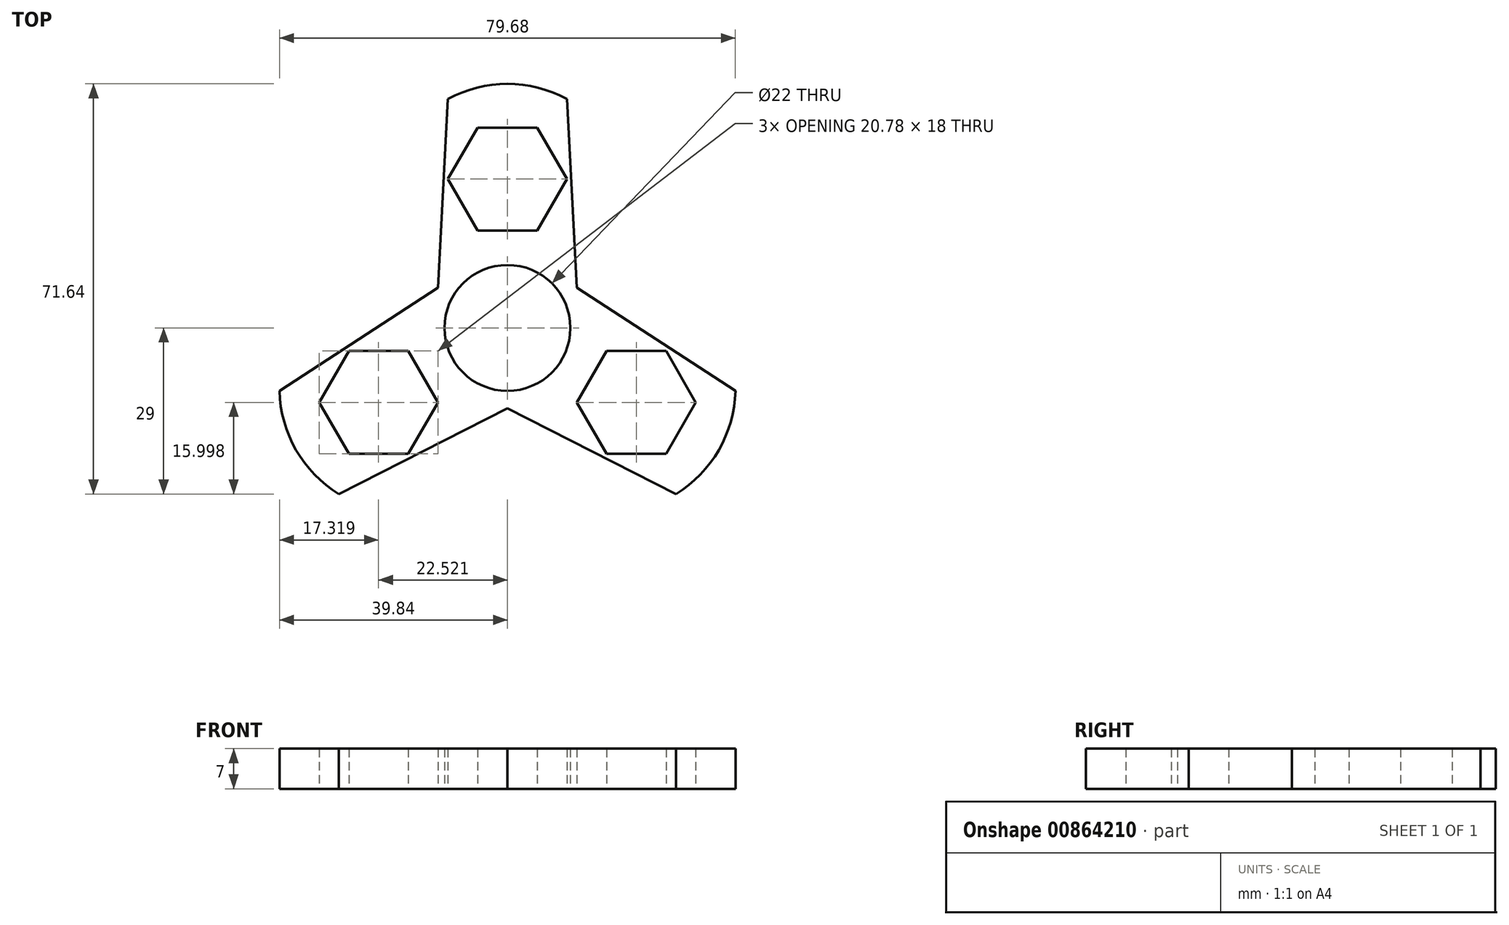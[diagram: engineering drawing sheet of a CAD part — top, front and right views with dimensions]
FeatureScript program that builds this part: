
annotation { "Feature Type Name" : "Feature", "Feature Type Description" : "" }
export const myFeature = defineFeature(function(context is Context, id is Id, definition is map)
    precondition{}
    {
        {
            var Q0;
            Q0=qCreatedBy(makeId("Top.planeOp"),FACE);
            var sketch = newSketch(context, id + "F0", { "sketchPlane" : qUnion([Q0])});
            skCircle(sketch, "E0", {"center": v(0, 0) * mm, "radius": 11 * mm});
            skCircle(sketch, "E1.0", {"center": v(0, 0) * mm, "radius": 14 * mm});
            skCircle(sketch, "E2", {"center": v(0, 0) * mm, "radius": 45 * mm, "construction": true});
            skLineSegment(sketch, "E3", {"start": v(-7.68, 21.31) * mm, "end": v(-7.68, 21.32) * mm});
            skLineSegment(sketch, "E4.MirrorCS", {"start": v(7.68, 21.31) * mm, "end": v(7.68, 21.32) * mm});
            skCircle(sketch, "E5.cCircle", {"center": v(0, 26) * mm, "radius": 9 * mm, "construction": true});
            skPoint(sketch, "E5.cCircle.centerSnap0", {"position": v(6.74, 26) * mm});
            skLineSegment(sketch, "E5.0", {"start": v(-5.2, 35) * mm, "end": v(5.2, 35) * mm});
            skLineSegment(sketch, "E5.1", {"start": v(5.2, 35) * mm, "end": v(10.4, 26) * mm});
            skLineSegment(sketch, "E5.2", {"start": v(10.4, 26) * mm, "end": v(5.2, 17) * mm});
            skLineSegment(sketch, "E5.3", {"start": v(5.2, 17) * mm, "end": v(-5.2, 17) * mm});
            skLineSegment(sketch, "E5.4", {"start": v(-5.2, 17) * mm, "end": v(-10.4, 26) * mm});
            skLineSegment(sketch, "E5.5", {"start": v(-10.4, 26) * mm, "end": v(-5.2, 35) * mm});
            skPoint(sketch, "E5.0.midPoint", {"position": v(0, 35) * mm});
            skLineSegment(sketch, "E6.trimOffspring", {"start": v(-5.28, 33.3) * mm, "end": v(-4.93, 35) * mm});
            skLineSegment(sketch, "E7.trimOffspring", {"start": v(5.28, 33.3) * mm, "end": v(4.93, 35) * mm});
            skPoint(sketch, "E8.start.orphan", {"position": v(-3.48, 42.2) * mm});
            skPoint(sketch, "E9.orphan", {"position": v(-10, 9.8) * mm});
            skPoint(sketch, "E10.orphan", {"position": v(10, 9.8) * mm});
            skPoint(sketch, "E11.orphan", {"position": v(3.48, 42.2) * mm});
            skPoint(sketch, "E12.end.orphan", {"position": v(-10.4, 40) * mm});
            skLineSegment(sketch, "E13", {"start": v(-12.15, 6.96) * mm, "end": v(-10.4, 40) * mm});
            skLineSegment(sketch, "E14.MirrorCS", {"start": v(12.15, 6.96) * mm, "end": v(10.4, 40) * mm});
            skArc(sketch, "E15", {"start": v(10.4, 40) * mm, "mid": v(0, 42.64) * mm, "end": v(-10.4, 40) * mm});
            skCircle(sketch, "E16.1.0", {"center": v(-22.52, -13) * mm, "radius": 9 * mm, "construction": true});
            skArc(sketch, "E16.1.1", {"start": v(-39.84, -11) * mm, "mid": v(-36.93, -21.32) * mm, "end": v(-29.45, -29) * mm});
            skLineSegment(sketch, "E16.1.2", {"start": v(0.04, -14) * mm, "end": v(-29.45, -29) * mm});
            skLineSegment(sketch, "E16.1.3", {"start": v(-12.1, 7.04) * mm, "end": v(-39.84, -11) * mm});
            skLineSegment(sketch, "E16.1.4", {"start": v(-17.32, -22) * mm, "end": v(-27.72, -22) * mm});
            skLineSegment(sketch, "E16.1.5", {"start": v(-12.13, -13) * mm, "end": v(-17.32, -22) * mm});
            skLineSegment(sketch, "E16.1.6", {"start": v(-17.32, -4) * mm, "end": v(-12.13, -13) * mm});
            skLineSegment(sketch, "E16.1.7", {"start": v(-27.72, -4) * mm, "end": v(-17.32, -4) * mm});
            skLineSegment(sketch, "E16.1.8", {"start": v(-32.91, -13) * mm, "end": v(-27.72, -4) * mm});
            skLineSegment(sketch, "E16.1.9", {"start": v(-27.72, -22) * mm, "end": v(-32.91, -13) * mm});
            skCircle(sketch, "E16.2.0", {"center": v(22.52, -13) * mm, "radius": 9 * mm, "construction": true});
            skArc(sketch, "E16.2.1", {"start": v(29.45, -29) * mm, "mid": v(36.93, -21.32) * mm, "end": v(39.84, -11) * mm});
            skLineSegment(sketch, "E16.2.2", {"start": v(12.1, 7.04) * mm, "end": v(39.84, -11) * mm});
            skLineSegment(sketch, "E16.2.3", {"start": v(-0.04, -14) * mm, "end": v(29.45, -29) * mm});
            skLineSegment(sketch, "E16.2.4", {"start": v(27.72, -4) * mm, "end": v(32.91, -13) * mm});
            skLineSegment(sketch, "E16.2.5", {"start": v(17.32, -4) * mm, "end": v(27.72, -4) * mm});
            skLineSegment(sketch, "E16.2.6", {"start": v(12.13, -13) * mm, "end": v(17.32, -4) * mm});
            skLineSegment(sketch, "E16.2.7", {"start": v(17.32, -22) * mm, "end": v(12.13, -13) * mm});
            skLineSegment(sketch, "E16.2.8", {"start": v(27.72, -22) * mm, "end": v(17.32, -22) * mm});
            skLineSegment(sketch, "E16.2.9", {"start": v(32.91, -13) * mm, "end": v(27.72, -22) * mm});
            skSolve(sketch);
        }
        {
            var Q0;
            Q0 = qSketchRegion(id + "F0", true);
            var Q1;
            Q1=makeQuery(id+"F0.imprint","IMPRINT",FACE,{"disambiguationData":[TD([[makeQuery(id+"F0.imprint","IMPRINT",EDGE,{"derivedFrom":sQuery(id+"F0.wireOp",EDGE,"E0")}),-1.0]])]});
            extrude(context, id + "F1", {"entities" : qUnion([Q0, Q1]), "depth" : 7 * mm, "offsetDistance" : 25 * mm});
        }
    });
